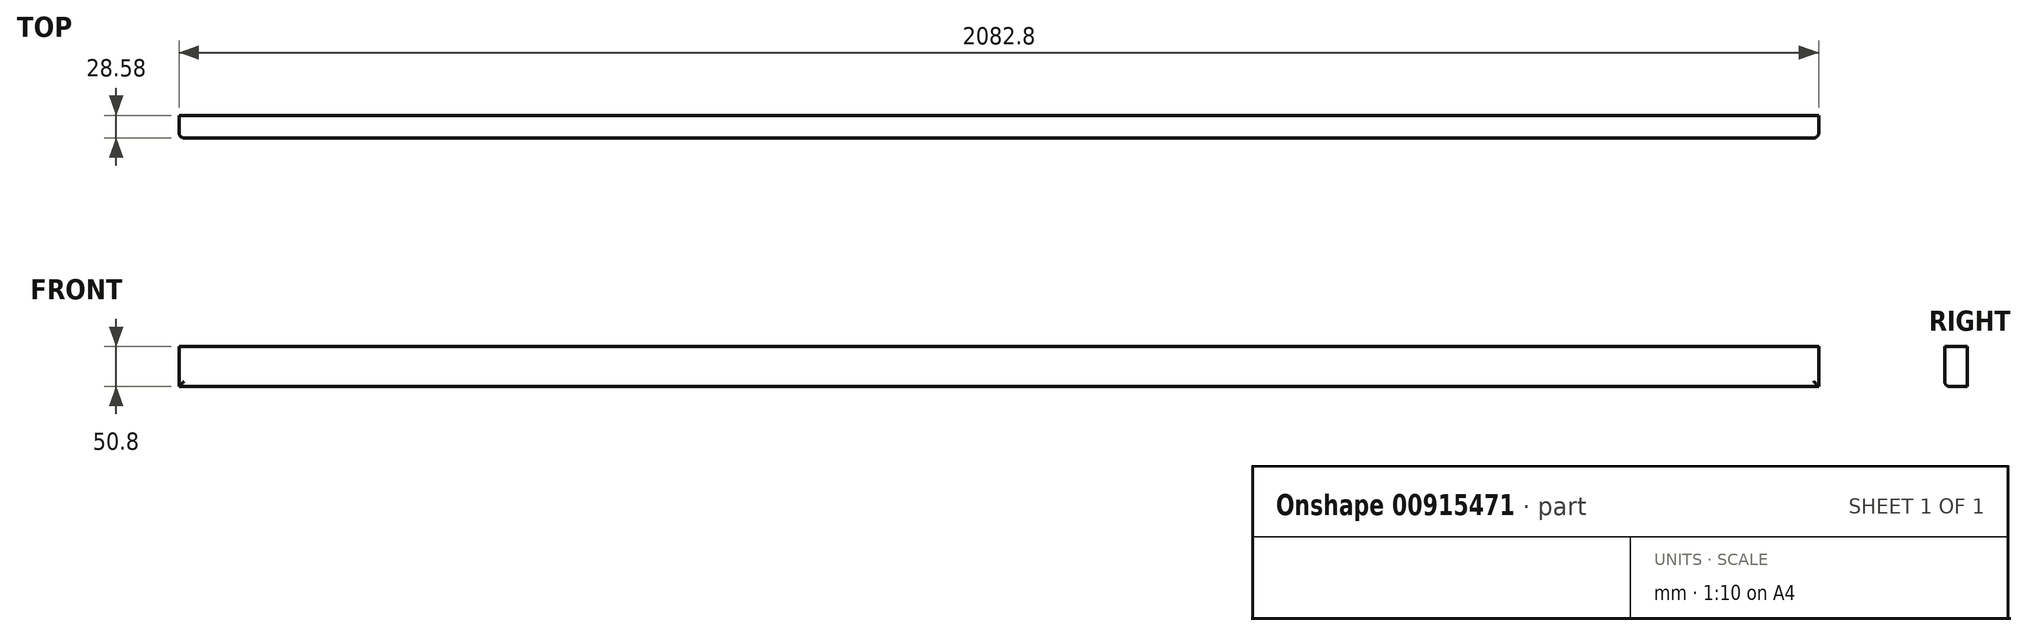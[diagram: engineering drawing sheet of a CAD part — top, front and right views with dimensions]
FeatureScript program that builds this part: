
annotation { "Feature Type Name" : "Feature", "Feature Type Description" : "" }
export const myFeature = defineFeature(function(context is Context, id is Id, definition is map)
    precondition{}
    {
        {
            var Q0;
            Q0=qCreatedBy(makeId("Right.planeOp"),FACE);
            var sketch = newSketch(context, id + "F0", { "sketchPlane" : qUnion([Q0])});
            skLineSegment(sketch, "E0.bottom", {"start": v(14.29, 25.4) * mm, "end": v(-14.29, 25.4) * mm});
            skLineSegment(sketch, "E0.top", {"start": v(14.29, -25.4) * mm, "end": v(-14.29, -25.4) * mm});
            skLineSegment(sketch, "E0.left", {"start": v(14.29, 25.4) * mm, "end": v(14.29, -25.4) * mm});
            skLineSegment(sketch, "E0.right", {"start": v(-14.29, 25.4) * mm, "end": v(-14.29, -25.4) * mm});
            skPoint(sketch, "E0.middle", {"position": v(0, 0) * mm});
            skSolve(sketch);
        }
        {
            var Q0;
            Q0=makeQuery(id+"F0.imprint","IMPRINT",FACE,{"disambiguationData":[TD([[makeQuery(id+"F0.imprint","IMPRINT",EDGE,{"derivedFrom":sQuery(id+"F0.wireOp",EDGE,"E0.bottom")}),1.0]])]});
            extrude(context, id + "F1", {"entities" : qUnion([Q0]), "depth" : 2082.8 * mm, "offsetDistance" : 25.4 * mm});
        }
        {
            var Q0;
            Q0=makeQuery(id+"F1.opExtrude","CAP_EDGE",EDGE,{"disambiguationData":[OSD([sQuery(id+"F0.wireOp",EDGE,"E0.right")])],"isStart":true});
            var Q1;
            Q1=makeQuery(id+"F1.opExtrude","SWEPT_EDGE",EDGE,{"disambiguationData":[OSD([sQuery(id+"F0.wireOp",EDGE,"E0.top"),sQuery(id+"F0.wireOp",EDGE,"E0.right")])]});
            var Q2;
            Q2=makeQuery(id+"F1.opExtrude","CAP_EDGE",EDGE,{"disambiguationData":[OSD([sQuery(id+"F0.wireOp",EDGE,"E0.right")])],"isStart":false});
            fillet(context, id + "F2", {"entities" : qUnion([Q0, Q1, Q2]), "radius" : 6.35 * mm, "tangentPropagation" : true, "allowEdgeOverflow" : false});
        }
    });
